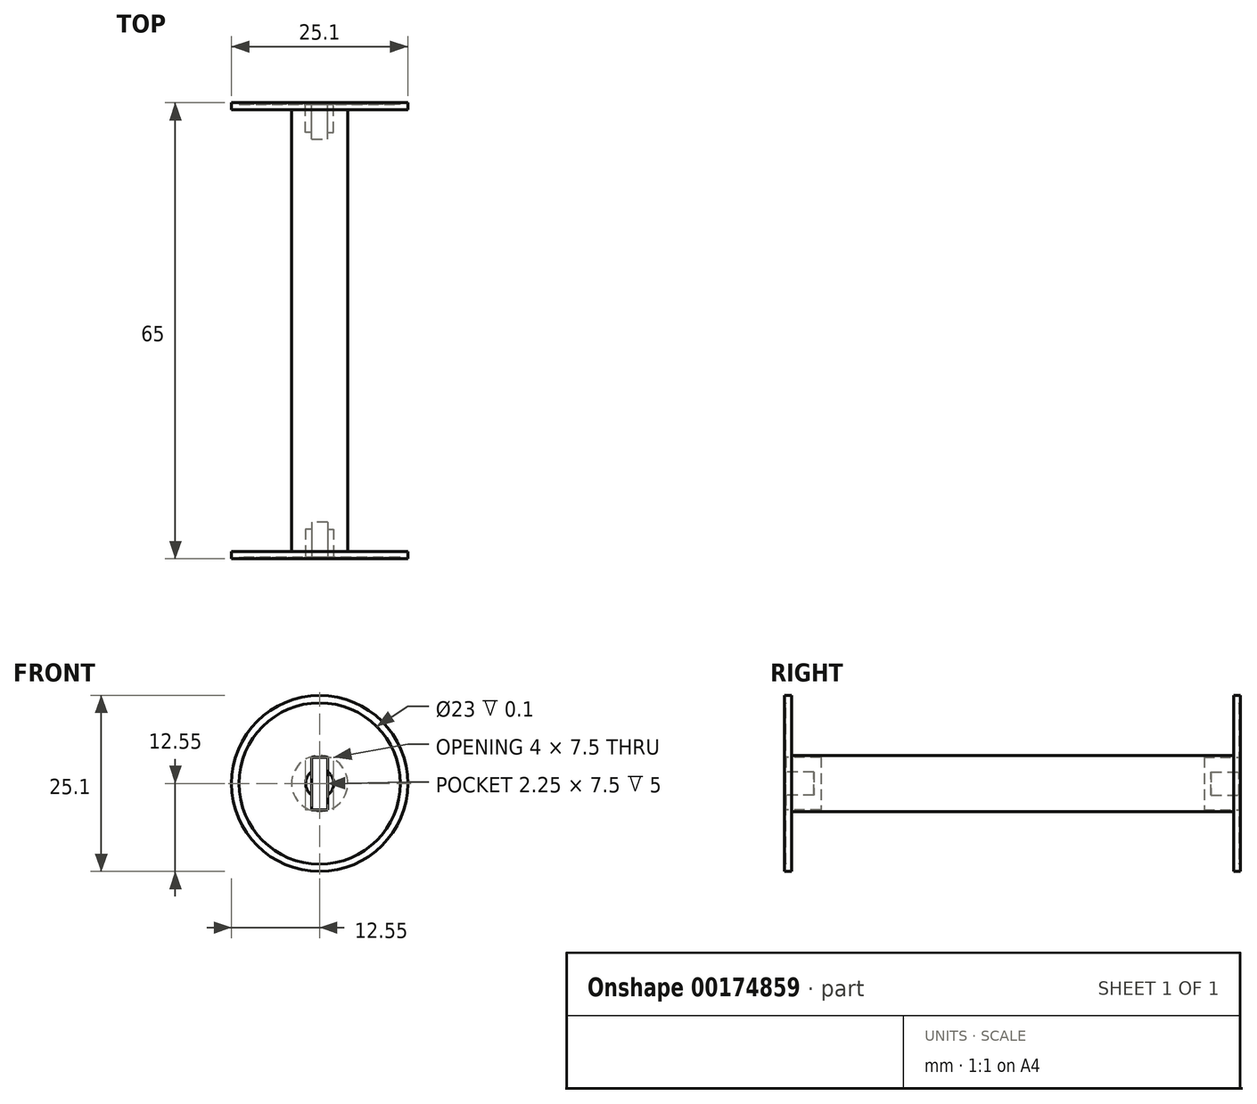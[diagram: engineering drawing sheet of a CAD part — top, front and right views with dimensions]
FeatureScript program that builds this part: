
annotation { "Feature Type Name" : "Feature", "Feature Type Description" : "" }
export const myFeature = defineFeature(function(context is Context, id is Id, definition is map)
    precondition{}
    {
        {
            var Q0;
            Q0=qCreatedBy(makeId("Front.planeOp"),FACE);
            var sketch = newSketch(context, id + "F0", { "sketchPlane" : qUnion([Q0])});
            skCircle(sketch, "E0", {"center": v(0, 0) * mm, "radius": 12.55 * mm});
            skSolve(sketch);
        }
        {
            var Q0;
            Q0 = qSketchRegion(id + "F0", true);
            extrude(context, id + "F1", {"entities" : qUnion([Q0]), "depth" : 1 * mm});
        }
        {
            var Q0;
            Q0=makeQuery(id+"F1.opExtrude","CAP_FACE",FACE,{"disambiguationData":[OSD([sQuery(id+"F0.wireOp",EDGE,"E0")])],"isStart":false});
            var sketch = newSketch(context, id + "F2", { "sketchPlane" : qUnion([Q0])});
            skCircle(sketch, "E1", {"center": v(0, 0) * mm, "radius": 4 * mm});
            skSolve(sketch);
        }
        {
            var Q0;
            Q0 = qSketchRegion(id + "F2", true);
            extrude(context, id + "F3", {"entities" : qUnion([Q0]), "operationType" : NewBodyOperationType.ADD, "depth" : 63 * mm});
        }
        {
            var Q0;
            Q0=makeQuery(id+"F3.opExtrude","CAP_FACE",FACE,{"disambiguationData":[OSD([sQuery(id+"F2.wireOp",EDGE,"E1")])],"isStart":false});
            var sketch = newSketch(context, id + "F4", { "sketchPlane" : qUnion([Q0])});
            skCircle(sketch, "E2", {"center": v(0, 0) * mm, "radius": 12.55 * mm});
            skSolve(sketch);
        }
        {
            var Q0;
            Q0 = qSketchRegion(id + "F4", true);
            extrude(context, id + "F5", {"entities" : qUnion([Q0]), "operationType" : NewBodyOperationType.ADD, "depth" : 1 * mm});
        }
        {
            var Q0;
            Q0=makeQuery(id+"F5.opExtrude","CAP_FACE",FACE,{"disambiguationData":[OSD([sQuery(id+"F4.wireOp",EDGE,"E2")])],"isStart":false});
            var sketch = newSketch(context, id + "F6", { "sketchPlane" : qUnion([Q0])});
            skCircle(sketch, "E3", {"center": v(0, 0) * mm, "radius": 11.5 * mm});
            skSolve(sketch);
        }
        {
            var Q0;
            Q0 = qSketchRegion(id + "F6", true);
            extrude(context, id + "F7", {"entities" : qUnion([Q0]), "operationType" : NewBodyOperationType.REMOVE, "oppositeDirection" : true, "depth" : .2 * mm});
        }
        {
            var Q0;
            Q0=makeQuery(id+"F7.boolean.opBoolean","COPY",EDGE,{"derivedFrom":makeQuery(id+"F7.opExtrude","CAP_EDGE",EDGE,{"disambiguationData":[OSD([sQuery(id+"F6.wireOp",EDGE,"E3")])],"isStart":true})});
            var Q1;
            Q1=makeQuery(id+"F7.boolean.opBoolean","COPY",FACE,{"derivedFrom":makeQuery(id+"F7.opExtrude","SWEPT_FACE",FACE,{"disambiguationData":[OSD([sQuery(id+"F6.wireOp",EDGE,"E3")])]})});
            fillet(context, id + "F8", {"entities" : qUnion([Q0, Q1]), "radius" : .1 * mm, "tangentPropagation" : true, "allowEdgeOverflow" : false});
        }
        {
            var Q0;
            Q0=makeQuery(id+"F7.boolean.opBoolean","COPY",FACE,{"derivedFrom":makeQuery(id+"F7.opExtrude","CAP_FACE",FACE,{"disambiguationData":[OSD([sQuery(id+"F6.wireOp",EDGE,"E3")])],"isStart":false})});
            var sketch = newSketch(context, id + "F9", { "sketchPlane" : qUnion([Q0])});
            skCircle(sketch, "E4", {"center": v(0, 0) * mm, "radius": 2 * mm});
            skSolve(sketch);
        }
        {
            var Q0;
            Q0 = qSketchRegion(id + "F9", true);
            extrude(context, id + "F10", {"entities" : qUnion([Q0]), "operationType" : NewBodyOperationType.REMOVE, "oppositeDirection" : true, "depth" : 4 * mm});
        }
        {
            var Q0;
            Q0=makeQuery(id+"F7.boolean.opBoolean","COPY",FACE,{"derivedFrom":makeQuery(id+"F7.opExtrude","CAP_FACE",FACE,{"disambiguationData":[OSD([sQuery(id+"F6.wireOp",EDGE,"E3")])],"isStart":false})});
            var sketch = newSketch(context, id + "F11", { "sketchPlane" : qUnion([Q0])});
            skLineSegment(sketch, "E5.bottom", {"start": v(1.13, 3.75) * mm, "end": v(-1.13, 3.75) * mm});
            skLineSegment(sketch, "E5.top", {"start": v(1.13, -3.75) * mm, "end": v(-1.13, -3.75) * mm});
            skLineSegment(sketch, "E5.left", {"start": v(1.13, 3.75) * mm, "end": v(1.13, -3.75) * mm});
            skLineSegment(sketch, "E5.right", {"start": v(-1.13, 3.75) * mm, "end": v(-1.13, -3.75) * mm});
            skPoint(sketch, "E5.middle", {"position": v(0, 0) * mm});
            skSolve(sketch);
        }
        {
            var Q0;
            Q0 = qSketchRegion(id + "F11", true);
            extrude(context, id + "F12", {"entities" : qUnion([Q0]), "operationType" : NewBodyOperationType.REMOVE, "oppositeDirection" : true, "depth" : 5 * mm});
        }
        {
            var Q0;
            Q0=makeQuery(id+"F1.opExtrude","CAP_FACE",FACE,{"disambiguationData":[OSD([sQuery(id+"F0.wireOp",EDGE,"E0")])],"isStart":true});
            var sketch = newSketch(context, id + "F13", { "sketchPlane" : qUnion([Q0])});
            skCircle(sketch, "E6", {"center": v(0, 0) * mm, "radius": 11.5 * mm});
            skSolve(sketch);
        }
        {
            var Q0;
            Q0 = qSketchRegion(id + "F13", true);
            extrude(context, id + "F14", {"entities" : qUnion([Q0]), "operationType" : NewBodyOperationType.REMOVE, "oppositeDirection" : true, "depth" : .2 * mm});
        }
        {
            var Q0;
            Q0=makeQuery(id+"F14.boolean.opBoolean","COPY",EDGE,{"derivedFrom":makeQuery(id+"F14.opExtrude","CAP_EDGE",EDGE,{"disambiguationData":[OSD([sQuery(id+"F13.wireOp",EDGE,"E6")])],"isStart":true})});
            var Q1;
            Q1=makeQuery(id+"F14.boolean.opBoolean","COPY",EDGE,{"derivedFrom":makeQuery(id+"F14.opExtrude","CAP_EDGE",EDGE,{"disambiguationData":[OSD([sQuery(id+"F13.wireOp",EDGE,"E6")])],"isStart":false})});
            fillet(context, id + "F15", {"entities" : qUnion([Q0, Q1]), "radius" : .1 * mm, "tangentPropagation" : true, "allowEdgeOverflow" : false});
        }
        {
            var Q0;
            Q0=makeQuery(id+"F14.boolean.opBoolean","COPY",FACE,{"derivedFrom":makeQuery(id+"F14.opExtrude","CAP_FACE",FACE,{"disambiguationData":[OSD([sQuery(id+"F13.wireOp",EDGE,"E6")])],"isStart":false})});
            var sketch = newSketch(context, id + "F16", { "sketchPlane" : qUnion([Q0])});
            skCircle(sketch, "E7", {"center": v(0, 0) * mm, "radius": 2 * mm});
            skSolve(sketch);
        }
        {
            var Q0;
            Q0 = qSketchRegion(id + "F16", true);
            extrude(context, id + "F17", {"entities" : qUnion([Q0]), "operationType" : NewBodyOperationType.REMOVE, "oppositeDirection" : true, "depth" : 4 * mm});
        }
        {
            var Q0;
            Q0=makeQuery(id+"F14.boolean.opBoolean","COPY",FACE,{"derivedFrom":makeQuery(id+"F14.opExtrude","CAP_FACE",FACE,{"disambiguationData":[OSD([sQuery(id+"F13.wireOp",EDGE,"E6")])],"isStart":false})});
            var sketch = newSketch(context, id + "F18", { "sketchPlane" : qUnion([Q0])});
            skLineSegment(sketch, "E8.bottom", {"start": v(1.12, 3.75) * mm, "end": v(-1.13, 3.75) * mm});
            skLineSegment(sketch, "E8.top", {"start": v(1.13, -3.75) * mm, "end": v(-1.12, -3.75) * mm});
            skLineSegment(sketch, "E8.left", {"start": v(1.12, 3.75) * mm, "end": v(1.13, -3.75) * mm});
            skLineSegment(sketch, "E8.right", {"start": v(-1.13, 3.75) * mm, "end": v(-1.12, -3.75) * mm});
            skPoint(sketch, "E8.middle", {"position": v(0, 0) * mm});
            skSolve(sketch);
        }
        {
            var Q0;
            Q0 = qSketchRegion(id + "F18", true);
            extrude(context, id + "F19", {"entities" : qUnion([Q0]), "operationType" : NewBodyOperationType.REMOVE, "oppositeDirection" : true, "depth" : 5 * mm});
        }
    });
